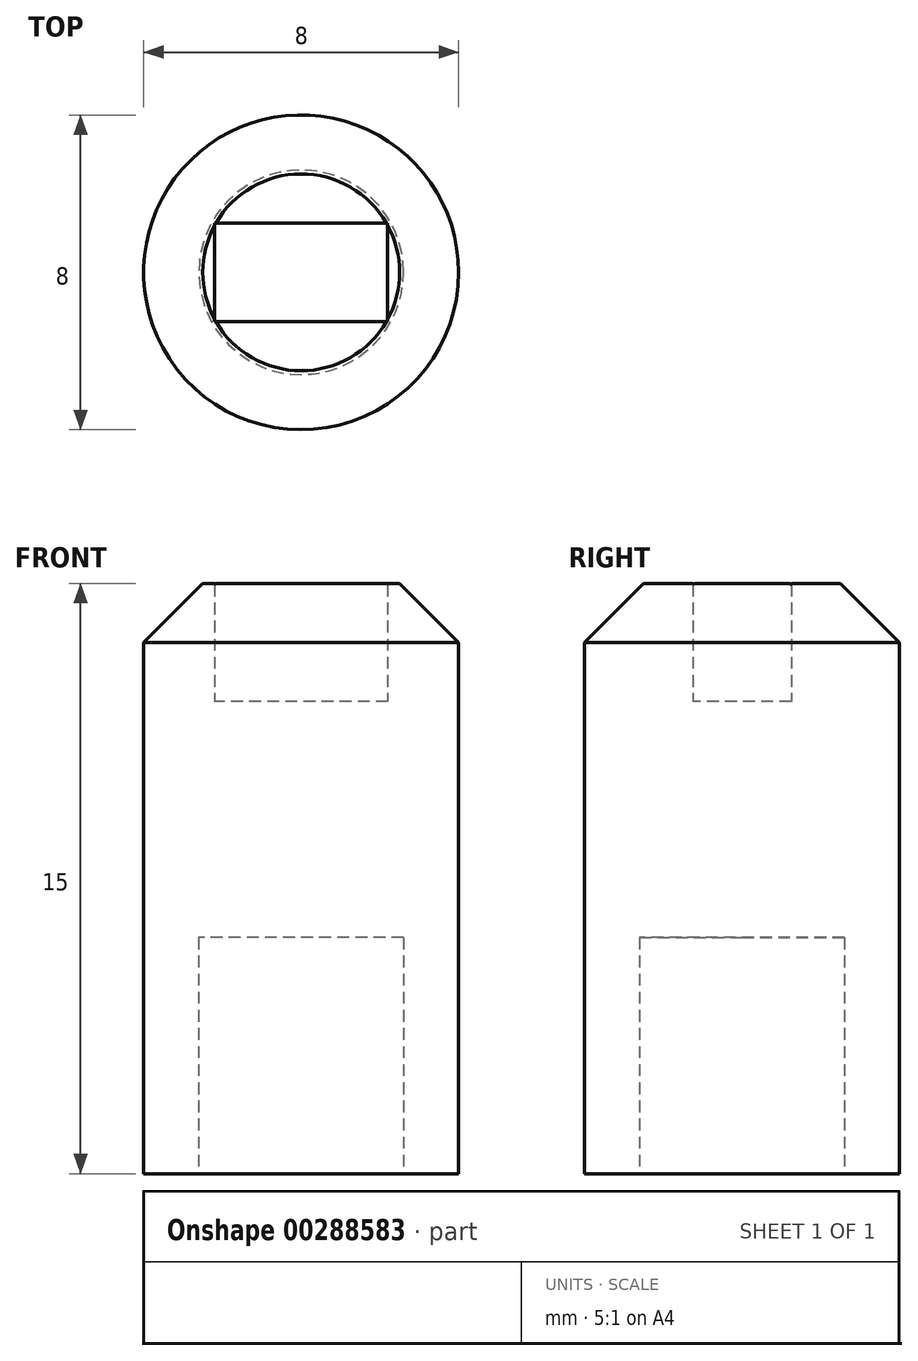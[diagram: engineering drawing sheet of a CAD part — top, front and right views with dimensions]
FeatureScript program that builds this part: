
annotation { "Feature Type Name" : "Feature", "Feature Type Description" : "" }
export const myFeature = defineFeature(function(context is Context, id is Id, definition is map)
    precondition{}
    {
        {
            var Q0;
            Q0=qCreatedBy(makeId("Top.planeOp"),FACE);
            var sketch = newSketch(context, id + "F0", { "sketchPlane" : qUnion([Q0])});
            skCircle(sketch, "E0", {"center": v(0, 0) * mm, "radius": 4 * mm});
            skCircle(sketch, "E1", {"center": v(0, 0) * mm, "radius": 2.6 * mm});
            skLineSegment(sketch, "E2.bottom", {"start": v(2.2, 1.25) * mm, "end": v(-2.2, 1.25) * mm});
            skLineSegment(sketch, "E2.top", {"start": v(2.2, -1.25) * mm, "end": v(-2.2, -1.25) * mm});
            skLineSegment(sketch, "E2.left", {"start": v(2.2, 1.25) * mm, "end": v(2.2, -1.25) * mm});
            skLineSegment(sketch, "E2.right", {"start": v(-2.2, 1.25) * mm, "end": v(-2.2, -1.25) * mm});
            skSolve(sketch);
        }
        {
            var Q0;
            Q0=makeQuery(id+"F0.imprint","IMPRINT",FACE,{"disambiguationData":[TD([[makeQuery(id+"F0.imprint","IMPRINT",EDGE,{"derivedFrom":sQuery(id+"F0.wireOp",EDGE,"E0")}),1.0]])]});
            extrude(context, id + "F1", {"entities" : qUnion([Q0]), "depth" : 15 * mm});
        }
        {
            var Q0;
            Q0=makeQuery(id+"F0.imprint","IMPRINT",FACE,{"disambiguationData":[TD([[makeQuery(id+"F0.imprint","IMPRINT",EDGE,{"derivedFrom":sQuery(id+"F0.wireOp",EDGE,"E1")}),1.0]])]});
            extrude(context, id + "F2", {"entities" : qUnion([Q0]), "operationType" : NewBodyOperationType.ADD, "depth" : 15 * mm, "hasSecondDirection" : true, "secondDirectionOppositeDirection" : false, "secondDirectionDepth" : 6 * mm});
        }
        {
            var Q0;
            Q0=makeQuery(id+"F0.imprint","IMPRINT",FACE,{"disambiguationData":[TD([[makeQuery(id+"F0.imprint","IMPRINT",EDGE,{"derivedFrom":sQuery(id+"F0.wireOp",EDGE,"E2.bottom")}),1.0]])]});
            extrude(context, id + "F3", {"entities" : qUnion([Q0]), "operationType" : NewBodyOperationType.ADD, "depth" : 12 * mm, "hasSecondDirection" : true, "secondDirectionOppositeDirection" : false, "secondDirectionDepth" : 6 * mm});
        }
        {
            var Q0;
            Q0=makeQuery(id+"F1.opExtrude","CAP_EDGE",EDGE,{"disambiguationData":[OSD([sQuery(id+"F0.wireOp",EDGE,"E0")])],"isStart":false});
            chamfer(context, id + "F4", {"entities" : qUnion([Q0]), "width" : 1.5 * mm, "tangentPropagation" : true});
        }
    });
